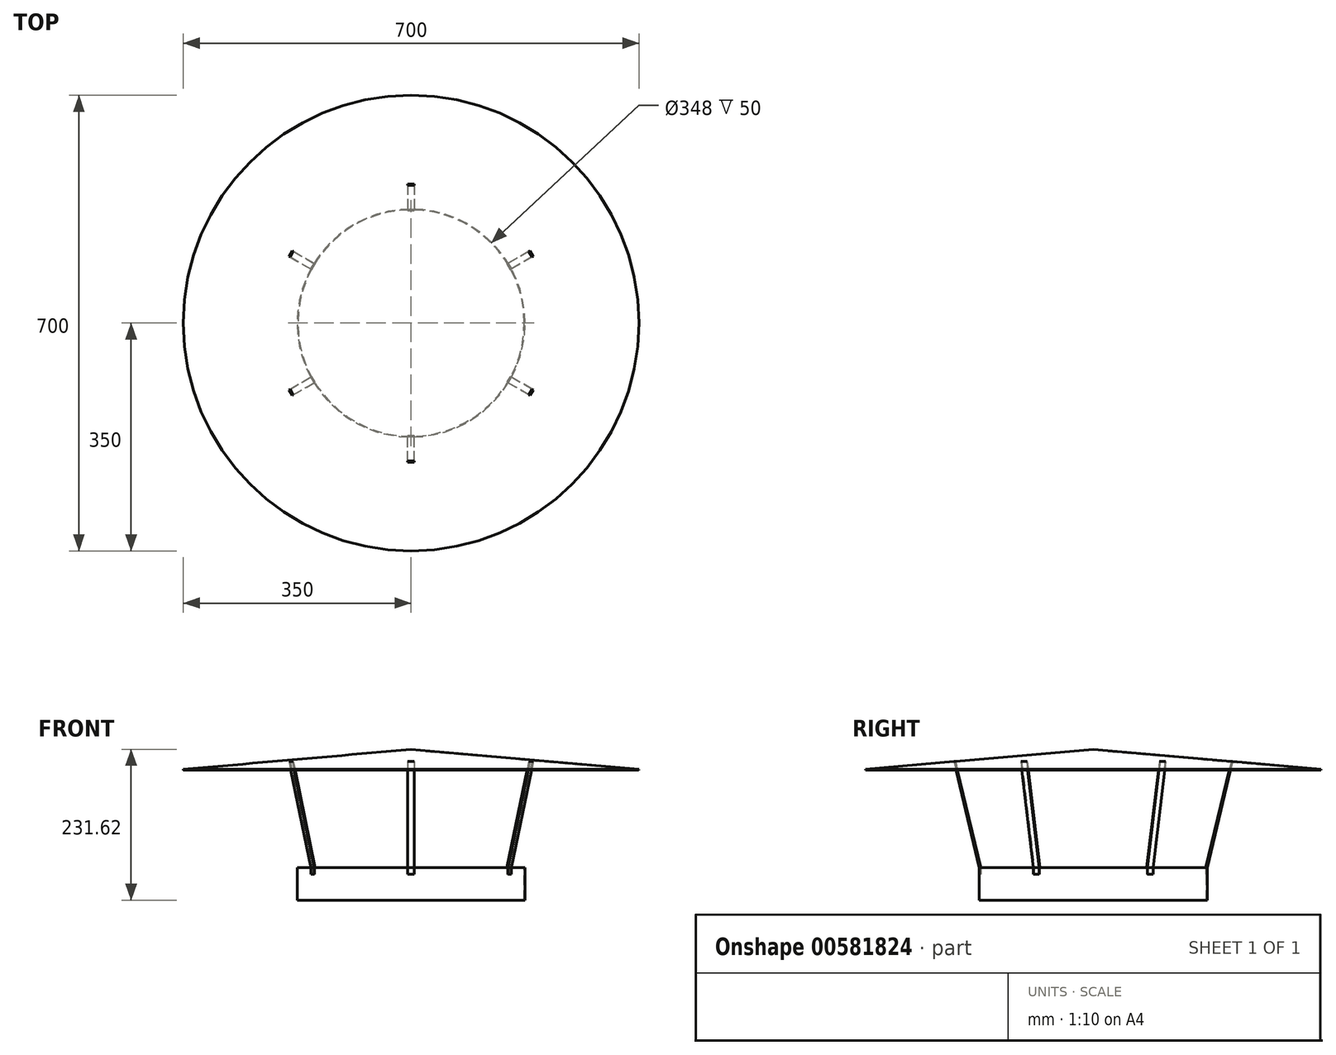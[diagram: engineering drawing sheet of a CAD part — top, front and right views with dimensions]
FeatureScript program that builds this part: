
annotation { "Feature Type Name" : "Feature", "Feature Type Description" : "" }
export const myFeature = defineFeature(function(context is Context, id is Id, definition is map)
    precondition{}
    {
        {
            var Q0;
            Q0=qCreatedBy(makeId("Top.planeOp"),FACE);
            var sketch = newSketch(context, id + "F0", { "sketchPlane" : qUnion([Q0])});
            skCircle(sketch, "E0", {"center": v(0, 0) * mm, "radius": 174 * mm});
            skCircle(sketch, "E1", {"center": v(0, 0) * mm, "radius": 175 * mm});
            skSolve(sketch);
        }
        {
            var Q0;
            Q0=qSketchRegion(id+"F0",true);
            extrude(context, id + "F1", {"entities" : qUnion([Q0]), "oppositeDirection" : true, "depth" : 50 * mm, "offsetDistance" : 25 * mm});
        }
        {
            var Q0;
            Q0=qCreatedBy(makeId("Right.planeOp"),FACE);
            var sketch = newSketch(context, id + "F2", { "sketchPlane" : qUnion([Q0])});
            skLineSegment(sketch, "E2", {"start": v(0, 0) * mm, "end": v(0, 181.62) * mm, "construction": true});
            skLineSegment(sketch, "E3", {"start": v(0, 181.62) * mm, "end": v(-350, 151) * mm});
            skLineSegment(sketch, "E4", {"start": v(-350, 151) * mm, "end": v(-349.91, 150) * mm});
            skLineSegment(sketch, "E5", {"start": v(-349.91, 150) * mm, "end": v(0, 180.61) * mm});
            skLineSegment(sketch, "E6", {"start": v(0, 180.61) * mm, "end": v(0, 181.62) * mm});
            skSolve(sketch);
        }
        {
            var Q0;
            Q0=qSketchRegion(id+"F2",true);
            var Q1;
            Q1=sQuery(id+"F2.wireOp",EDGE,"E2");
            revolve(context, id + "F3", {"surfaceOperationType" : NewSurfaceOperationType.NEW, "entities" : qUnion([Q0]), "axis" : qUnion([Q1]), "revolveType" : RevolveType.FULL});
        }
        {
            var Q0;
            Q0=qCreatedBy(makeId("Right.planeOp"),FACE);
            var sketch = newSketch(context, id + "F4", { "sketchPlane" : qUnion([Q0])});
            skLineSegment(sketch, "E7.0", {"start": v(-175, 0) * mm, "end": v(175, 0) * mm, "construction": true});
            skLineSegment(sketch, "E8", {"start": v(-175, -50) * mm, "end": v(-175, 0) * mm, "construction": true});
            skLineSegment(sketch, "E9", {"start": v(-300.38, 155.34) * mm, "end": v(-0.38, 181.58) * mm, "construction": true});
            skLineSegment(sketch, "E10", {"start": v(-211.77, 163.09) * mm, "end": v(-213.73, 162.92) * mm});
            skLineSegment(sketch, "E11", {"start": v(-213.73, 162.92) * mm, "end": v(-175, 0) * mm});
            skLineSegment(sketch, "E12", {"start": v(-211.77, 163.09) * mm, "end": v(-173, 0) * mm});
            skLineSegment(sketch, "E13", {"start": v(-173, 0) * mm, "end": v(-173, -10) * mm});
            skLineSegment(sketch, "E14", {"start": v(-173, -10) * mm, "end": v(-175, -10) * mm});
            skLineSegment(sketch, "E15", {"start": v(-175, -10) * mm, "end": v(-175, 0) * mm});
            skSolve(sketch);
        }
        {
            var Q0;
            Q0=qSketchRegion(id+"F4",true);
            extrude(context, id + "F5", {"entities" : qUnion([Q0]), "depth" : 10 * mm, "offsetDistance" : 25 * mm, "symmetric" : true});
        }
        {
            var Q0;
            Q0=qCreatedBy(makeId("Right.planeOp"),FACE);
            var sketch = newSketch(context, id + "F6", { "sketchPlane" : qUnion([Q0])});
            skLineSegment(sketch, "E16", {"start": v(0, 0) * mm, "end": v(0, 275.74) * mm, "construction": true});
            skSolve(sketch);
        }
        {
            var Q0;
            Q0=makeQuery(id+"F5.opExtrude","SWEPT_BODY",BODY,{"disambiguationData":[OSD([sQuery(id+"F4.wireOp",EDGE,"sHu2Gir7-9ggc-A0BL-dRGA-Pvlho7gEY1Av"),sQuery(id+"F4.wireOp",EDGE,"E10"),sQuery(id+"F4.wireOp",EDGE,"E11"),sQuery(id+"F4.wireOp",EDGE,"4oHM4HFf-rFhq-OT9C-b5np-XKB4EdHShkcs"),sQuery(id+"F4.wireOp",EDGE,"343eP1Ns-5I6F-shWL-LBzT-Atdx6hGGUzft"),sQuery(id+"F4.wireOp",EDGE,"I0gdIfue-qcDF-GefX-ffwp-bMTbIkreWT4E")])]});
            var Q1;
            Q1=sQuery(id+"F6.wireOp",EDGE,"E16");
            circularPattern(context, id + "F7", {"entities" : qUnion([Q0]), "axis" : qUnion([Q1]), "angle" : 360 * degree, "instanceCount" : 6, "equalSpace" : true, "computeTransformsWithoutBuiltin" : true});
        }
    });
